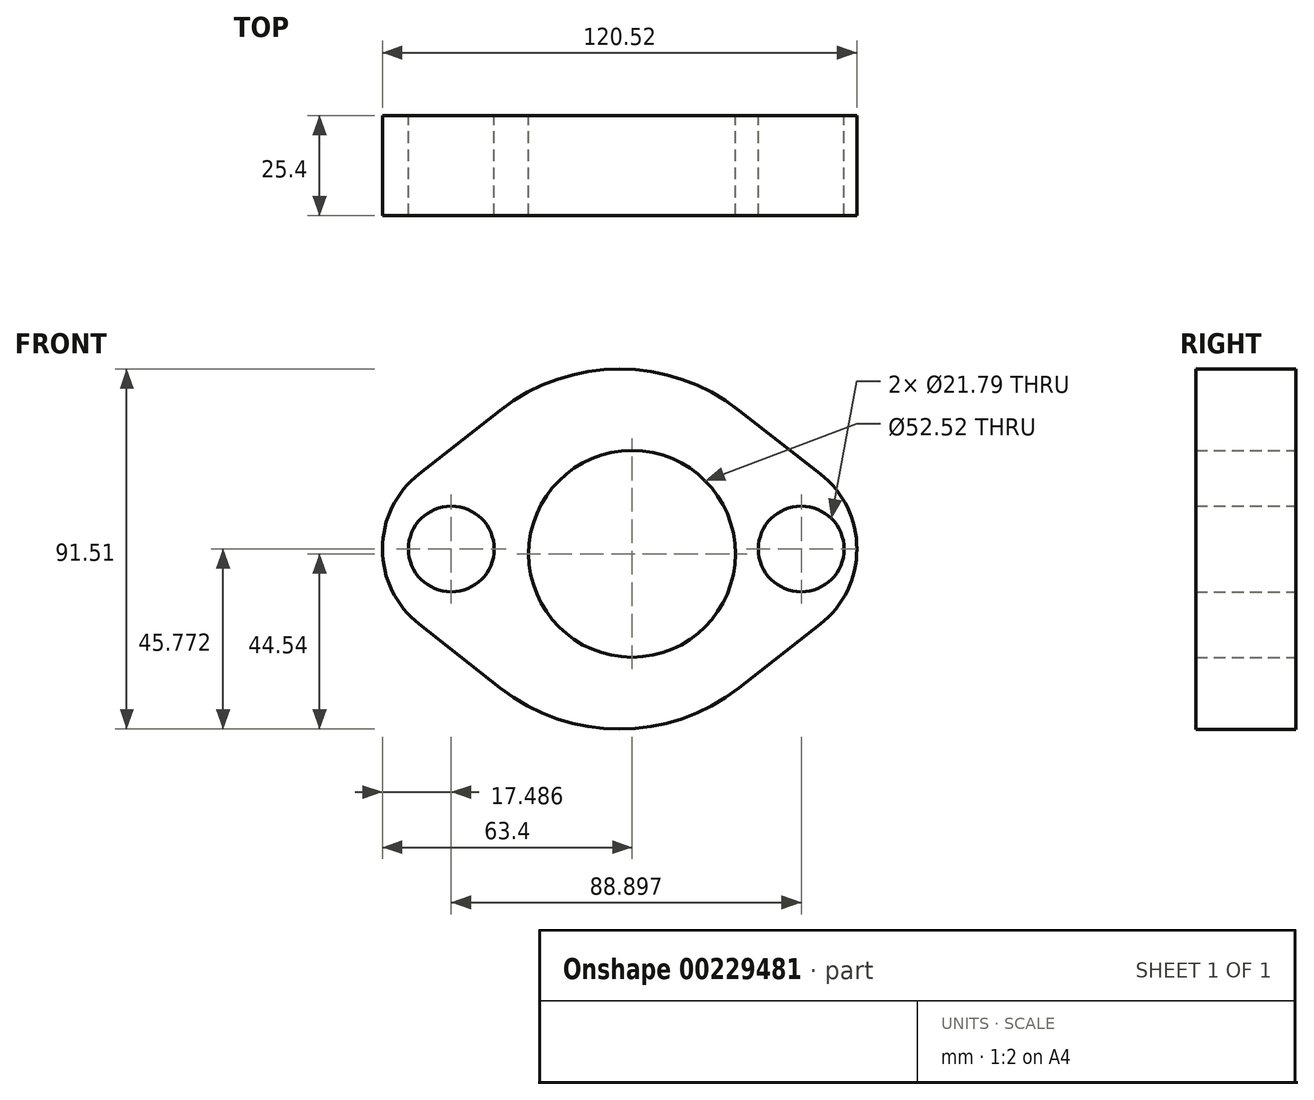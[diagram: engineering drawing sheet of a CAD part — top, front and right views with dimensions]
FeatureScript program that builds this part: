
annotation { "Feature Type Name" : "Feature", "Feature Type Description" : "" }
export const myFeature = defineFeature(function(context is Context, id is Id, definition is map)
    precondition{}
    {
        {
            var Q0;
            Q0=qCreatedBy(makeId("Front.planeOp"),FACE);
            var sketch = newSketch(context, id + "F0", { "sketchPlane" : qUnion([Q0])});
            skArc(sketch, "E0", {"start": v(27.22, 36.48) * mm, "mid": v(-3.14, 46.97) * mm, "end": v(-33.5, 36.48) * mm});
            skLineSegment(sketch, "E1", {"start": v(-33.5, 36.48) * mm, "end": v(-54.1, 20.32) * mm});
            skLineSegment(sketch, "E2", {"start": v(27.22, 36.48) * mm, "end": v(47.83, 20.32) * mm});
            skArc(sketch, "E3", {"start": v(-54.1, 20.32) * mm, "mid": v(-63.4, 1.23) * mm, "end": v(-54.1, -17.86) * mm});
            skArc(sketch, "E4", {"start": v(47.83, -17.86) * mm, "mid": v(57.12, 1.23) * mm, "end": v(47.83, 20.32) * mm});
            skLineSegment(sketch, "E5", {"start": v(-54.1, -17.86) * mm, "end": v(-33.5, -34.02) * mm});
            skLineSegment(sketch, "E6", {"start": v(47.83, -17.86) * mm, "end": v(27.13, -34.1) * mm});
            skArc(sketch, "E7", {"start": v(-33.5, -34.02) * mm, "mid": v(-3.2, -44.54) * mm, "end": v(27.13, -34.1) * mm});
            skCircle(sketch, "E8", {"center": v(0, 0) * mm, "radius": 26.26 * mm});
            skCircle(sketch, "E9", {"center": v(-45.91, 1.23) * mm, "radius": 10.9 * mm});
            skCircle(sketch, "E10", {"center": v(42.98, 1.23) * mm, "radius": 10.9 * mm});
            skSolve(sketch);
        }
        {
            var Q0;
            Q0 = qSketchRegion(id + "F0", true);
            extrude(context, id + "F1", {"entities" : qUnion([Q0]), "depth" : 25.4 * mm});
        }
    });
